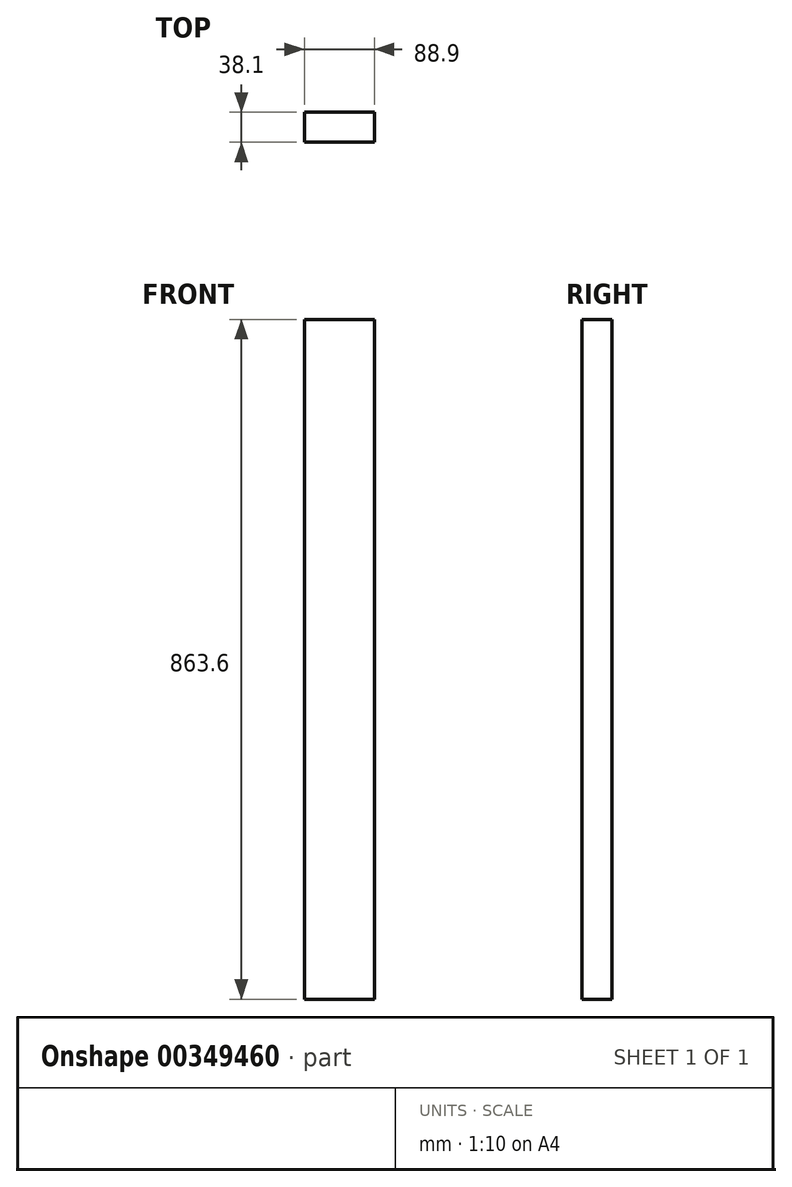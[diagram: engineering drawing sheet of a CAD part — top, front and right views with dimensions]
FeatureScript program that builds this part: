
annotation { "Feature Type Name" : "Feature", "Feature Type Description" : "" }
export const myFeature = defineFeature(function(context is Context, id is Id, definition is map)
    precondition{}
    {
        {
            var Q0;
            Q0=qCreatedBy(makeId("Top.planeOp"),FACE);
            var sketch = newSketch(context, id + "F0", { "sketchPlane" : qUnion([Q0])});
            skLineSegment(sketch, "E0.bottom", {"start": v(-36.95, 8.15) * mm, "end": v(51.95, 8.15) * mm});
            skLineSegment(sketch, "E0.top", {"start": v(-36.95, -29.95) * mm, "end": v(51.95, -29.95) * mm});
            skLineSegment(sketch, "E0.left", {"start": v(-36.95, 8.15) * mm, "end": v(-36.95, -29.95) * mm});
            skLineSegment(sketch, "E0.right", {"start": v(51.95, 8.15) * mm, "end": v(51.95, -29.95) * mm});
            skSolve(sketch);
        }
        {
            var Q0;
            Q0=makeQuery(id+"F0.imprint","IMPRINT",FACE,{"disambiguationData":[TD([[makeQuery(id+"F0.imprint","IMPRINT",EDGE,{"derivedFrom":sQuery(id+"F0.wireOp",EDGE,"E0.bottom")}),-1.0]])]});
            extrude(context, id + "F1", {"entities" : qUnion([Q0]), "depth" : 863.6 * mm});
        }
    });
